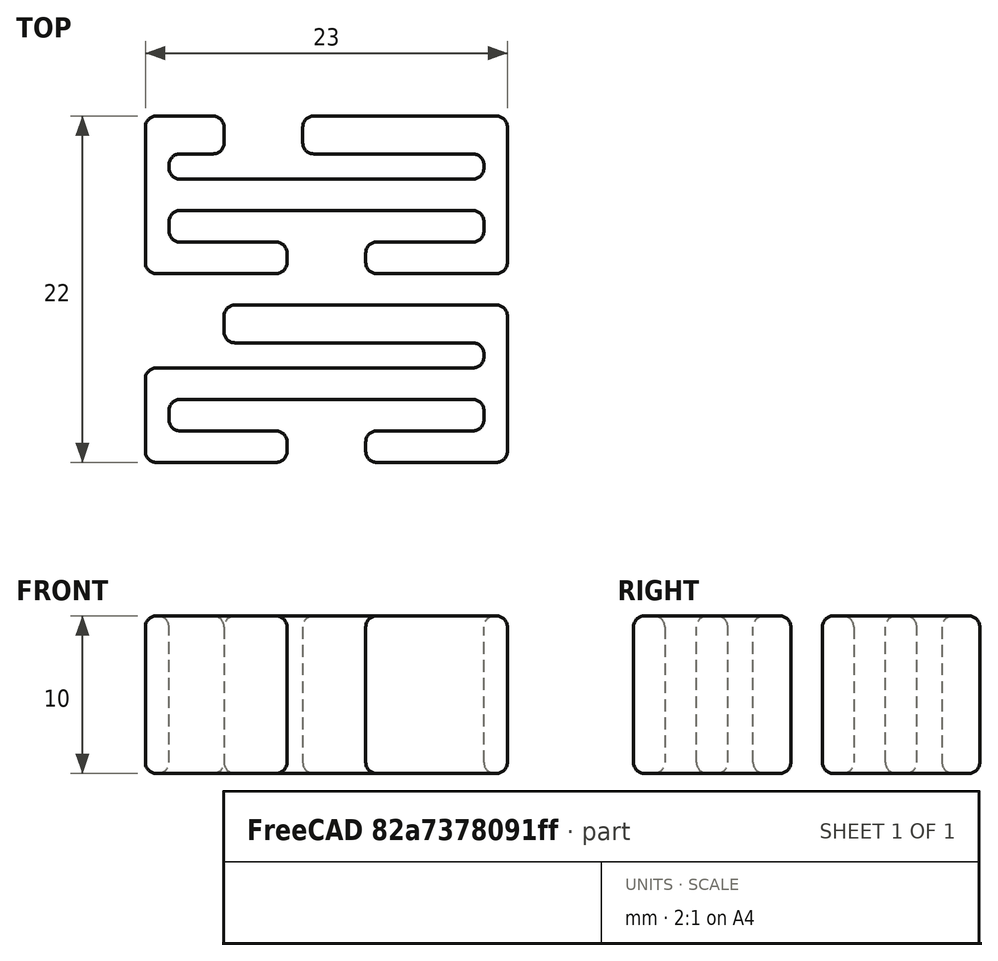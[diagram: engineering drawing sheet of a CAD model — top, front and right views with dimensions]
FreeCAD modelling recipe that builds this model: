
FCSTD DOCUMENT  (FreeCAD 0.16R6706 (Git))
Label: clip_mochila_20mm
License: CC-BY 3.0
LicenseURL: http://creativecommons.org/licenses/by/3.0/
objects: Part::Box×10, Part::Cut×8, Part::Fillet×2
note: 20 computed .brp shape members not serialized (recipe doc carries the construction recipe); baked Part::Feature solids carry a one-line shape summary decoded from their .brp

FEATURE [Part::Box] Box005  label="ext001"
  Height = 10
  Length = 23
  Width = 10
FEATURE [Part::Box] Box006  label="Cubo006"
  Height = 10
  Length = 20
  Placement = pos=(1.5,6,0) rot=(0,0,1;0rad)
  Width = 1.6
FEATURE [Part::Box] Box007  label="Cubo007"
  Height = 10
  Length = 20
  Placement = pos=(1.5,2,0) rot=(0,0,1;0rad)
  Width = 2
FEATURE [Part::Box] Box008  label="Cubo008"
  Height = 10
  Length = 5
  Placement = pos=(9,0,0) rot=(0,0,1;0rad)
  Width = 2.5
FEATURE [Part::Box] Box014  label="Cubo013"
  Height = 10
  Length = 5
  Placement = pos=(5,7.5,0) rot=(0,0,1;0rad)
  Width = 3
FEATURE [Part::Cut] Cut
  Base = -> Box005
  Tool = -> Box006
FEATURE [Part::Cut] Cut001
  Base = -> Cut
  Tool = -> Box007
FEATURE [Part::Cut] Cut002
  Base = -> Cut001
  Tool = -> Box008
FEATURE [Part::Cut] Cut003
  Base = -> Cut002
  Tool = -> Box014
FEATURE [Part::Box] Box015  label="ext002"
  Height = 10
  Length = 23
  Width = 10
FEATURE [Part::Box] Box016  label="Cubo014"
  Height = 10
  Length = 20
  Placement = pos=(1.5,6,0) rot=(0,0,1;0rad)
  Width = 1.6
FEATURE [Part::Box] Box017  label="Cubo015"
  Height = 10
  Length = 20
  Placement = pos=(1.5,2,0) rot=(0,0,1;0rad)
  Width = 2
FEATURE [Part::Box] Box018  label="Cubo016"
  Height = 10
  Length = 5
  Placement = pos=(9,0,0) rot=(0,0,1;0rad)
  Width = 2.5
FEATURE [Part::Box] Box019  label="Cubo017"
  Height = 10
  Length = 5
  Placement = pos=(0,6,0) rot=(0,0,1;0rad)
  Width = 4
FEATURE [Part::Cut] Cut004
  Base = -> Box015
  Tool = -> Box016
FEATURE [Part::Cut] Cut005
  Base = -> Cut004
  Tool = -> Box017
FEATURE [Part::Cut] Cut006
  Base = -> Cut005
  Tool = -> Box018
FEATURE [Part::Cut] Cut007
  Base = -> Cut006
  Placement = pos=(0,-12,0) rot=(0,0,1;0rad)
  Tool = -> Box019
FEATURE [Part::Fillet] Fillet
  Base = -> Cut003
  Edges = 60 edges r=0.7: [Edge1,Edge2,Edge3,Edge4,Edge5,Edge6,Edge7,Edge8,Edge9,Edge10,Edge11,Edge12,Edge13,Edge14,Edge15,Edge16,Edge17,Edge18,Edge19,Edge20,Edge21,Edge22,Edge23,Edge24,Edge25,Edge26,Edge27,Edge28,Edge29,Edge30,Edge31,Edge32,Edge33,Edge34,Edge35,Edge36,Edge37,Edge38,Edge39,Edge40,Edge41,Edge42,Edge43,Edge44,+16 more]
FEATURE [Part::Fillet] Fillet001
  Base = -> Cut007
  Edges = 54 edges r=0.7: [Edge1,Edge2,Edge3,Edge4,Edge5,Edge6,Edge7,Edge8,Edge9,Edge10,Edge11,Edge12,Edge13,Edge14,Edge15,Edge16,Edge17,Edge18,Edge19,Edge20,Edge21,Edge22,Edge23,Edge24,Edge25,Edge26,Edge27,Edge28,Edge29,Edge30,Edge31,Edge32,Edge33,Edge34,Edge35,Edge36,Edge37,Edge38,Edge39,Edge40,Edge41,Edge42,Edge43,Edge44,+10 more]
